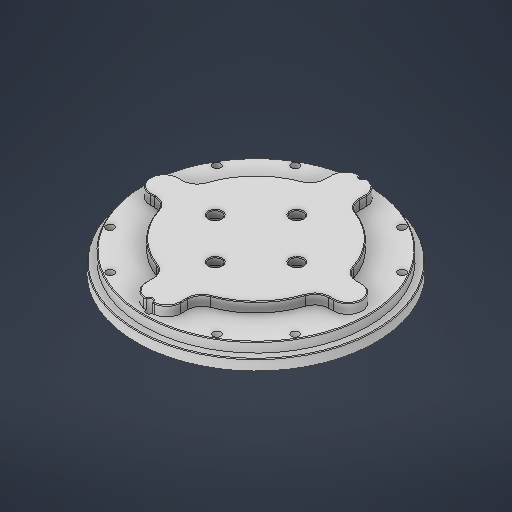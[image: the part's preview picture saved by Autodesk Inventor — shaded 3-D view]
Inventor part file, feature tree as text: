
AUTODESK INVENTOR PART (.ipt)
format: ipt  version: 2025 (Build 290162000, 162)  size: 571,392 bytes
history: native  units: in
note: dims shown in document units (in); Inventor stores cm internally (conversion verified against a paired STEP export)
features: sketch x11, extrude x8, hole x4, chamfer x2
ambient origin geometry x8: Origin, YZ Plane, XZ Plane, XY Plane, X Axis, Y Axis, Z Axis, Center Point
bodies: Solid1 (feature_tree)
feature tree (25):
  sketch  "Sketch1"  dims[d3=4.3307in d24=6.6929in]
  extrude  "Extrusion1"  Depth=6.6929in
  extrude  "Extrusion2"  Depth=5.9843in
  extrude  "Extrusion3"  Depth=4.3307in
  sketch  "Sketch2"  dims[d27=0.9843in d28=4.3307in]
  extrude  "Extrusion4"  Depth=0.3937in
  hole  "Hole1"  [1 undecoded]
  hole  "Hole2"  [1 undecoded]
  sketch  "Sketch4"  dims[d38=0.2953in d39=0.0in d40=2.2835in]
  extrude  "Extrusion5"  Depth=2.2835in
  extrude  "Extrusion6"  Depth=0.1969in
  hole  "Hole3"  [1 undecoded]
  chamfer  "Chamfer1"  Distance=0.1378in
  chamfer  "Chamfer2"  Distance=0.7874in Angle=360.0deg
  hole  "Hole5"  [1 undecoded]
  sketch  "Sketch8"  dims[d56=5.9843in d57=0.1378in d58=0.7874in d60=360.0deg d62=0.1772in d63=0.315in d64=0.1575in d65=0.0787in d66=90.0deg d67=0.4646in d68=0.8108in d69=3.1496in d70=0.1969in d71=0.7874in d72=0.0591in d73=0.0in d74=0.4724in d75=0.0in d76=0.1969in d77=4.7244in d79=360.0deg d81=0.2165in d82=0.3937in d83=0.1575in d84=0.0787in d85=90.0deg d86=0.3937in d87=0.8108in d88=0.0197in d89=0.0787in d90=45.0deg d91=0.0197in d92=0.0787in d93=45.0deg d107=3.7402in d108=0.1969in d109=6.2992in d111=360.0deg d113=0.1969in d114=0.7874in d115=0.748in d116=0.3543in d117=90.0deg d118=0.7874in d119=0.8108in d120=0.3051in d121=0.3051in d122=0.3051in d123=0.3051in d125=0.3051in d126=0.3051in d127=0.3051in d128=0.3051in d129=0.3051in d130=0.3051in d131=0.3051in d132=0.3051in d133=0.2854in d134=0.2854in d135=0.1575in d136=0.0in d137=0.1378in d138=0.0in d139=0.0197in d140=0.0344in]
  extrude  "Extrusion7"  Depth=0.0197in
  extrude  "Extrusion8"  Depth=0.0197in
  sketch  "Sketch Circular Pattern1"  dims[d25=6.2992in d26=5.9843in]
  sketch  "Sketch3"  dims[d31=0.3937in d32=0.3937in]
  sketch  "Sketch Circular Pattern2"  dims[d29=0.7874in d30=0.3937in]
  sketch  "Sketch5"  dims[d41=0.3543in d42=0.1969in]
  sketch  "Sketch Circular Pattern3"  dims[d34=0.8465in d35=0.0in d36=0.5709in d37=0.0in]
  sketch  "Sketch7"  dims[d49=0.2165in d50=0.7874in d51=0.1575in d52=0.0787in d53=90.0deg d54=0.315in d55=0.8108in]
  sketch  "Sketch Circular Pattern5"  dims[d43=1.5748in d45=360.0deg d47=0.1969in d48=0.0in]
note: 4 required parameter values undecoded (feature->parameter linkage not recoverable at this tier; creation-order binding heuristic only, values carry confidence <= 0.55)
